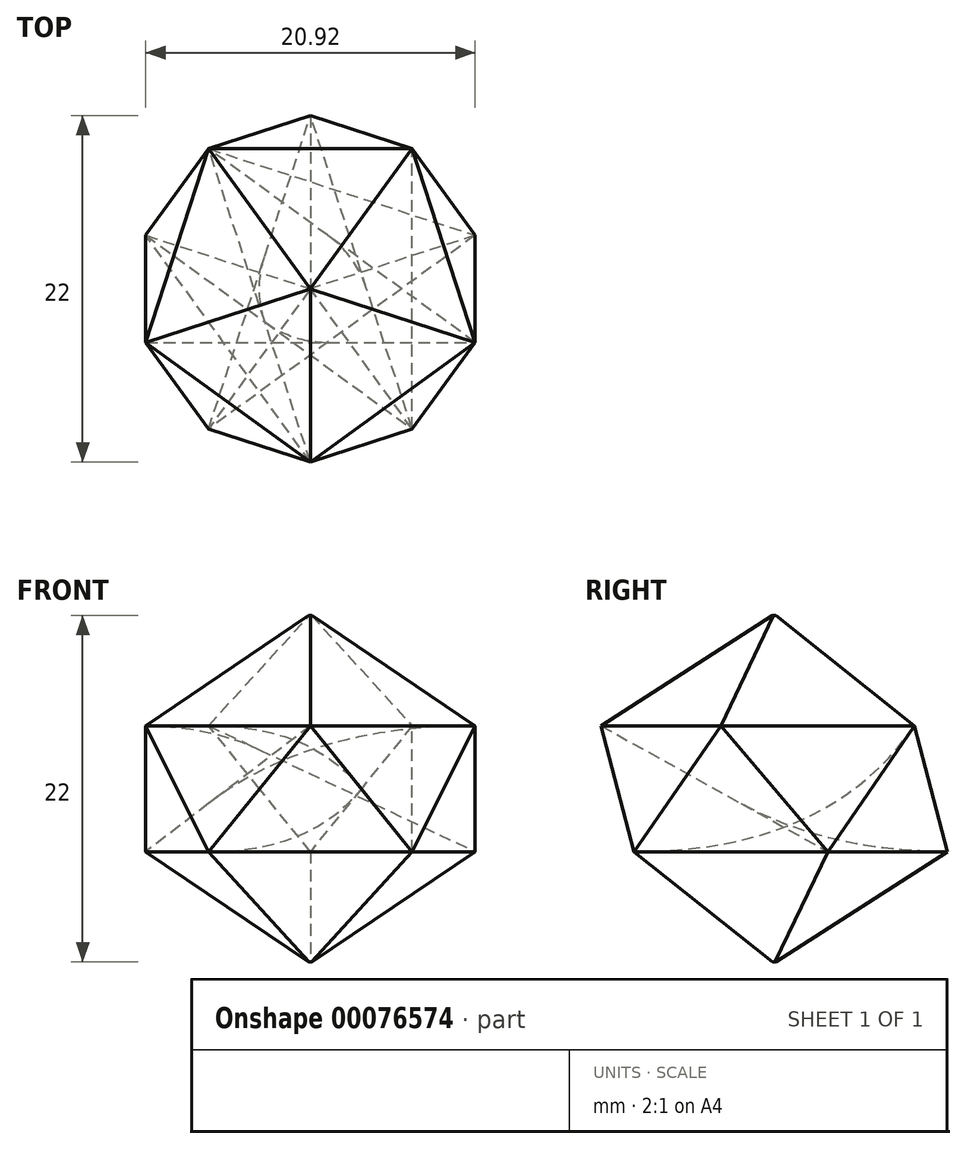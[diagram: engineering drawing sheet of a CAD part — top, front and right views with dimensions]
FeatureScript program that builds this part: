
annotation { "Feature Type Name" : "Feature", "Feature Type Description" : "" }
export const myFeature = defineFeature(function(context is Context, id is Id, definition is map)
    precondition{}
    {
        {
            var Q0;
            Q0=qCreatedBy(makeId("Top.planeOp"),FACE);
            var sketch = newSketch(context, id + "F0", { "sketchPlane" : qUnion([Q0])});
            skCircle(sketch, "E0.cCircle", {"center": v(0, 0) * mm, "radius": 11 * mm, "construction": true});
            skLineSegment(sketch, "E0.0", {"start": v(-6.47, 8.9) * mm, "end": v(6.47, 8.9) * mm});
            skLineSegment(sketch, "E0.1", {"start": v(6.47, 8.9) * mm, "end": v(10.46, -3.4) * mm});
            skLineSegment(sketch, "E0.2", {"start": v(10.46, -3.4) * mm, "end": v(0, -11) * mm});
            skLineSegment(sketch, "E0.3", {"start": v(0, -11) * mm, "end": v(-10.46, -3.4) * mm});
            skLineSegment(sketch, "E0.4", {"start": v(-10.46, -3.4) * mm, "end": v(-6.47, 8.9) * mm});
            skSolve(sketch);
        }
        {
            var Q0;
            Q0=makeQuery(id+"F0.imprint","IMPRINT",FACE,{"disambiguationData":[TD([[makeQuery(id+"F0.imprint","IMPRINT",EDGE,{"derivedFrom":sQuery(id+"F0.wireOp",EDGE,"E0.0")}),-1.0]])]});
            extrude(context, id + "F1", {"entities" : qUnion([Q0]), "depth" : 7 * mm});
        }
        {
            var Q0;
            Q0=makeQuery(id+"F1.opExtrude","CAP_FACE",FACE,{"disambiguationData":[OSD([sQuery(id+"F0.wireOp",EDGE,"E0.0"),sQuery(id+"F0.wireOp",EDGE,"E0.1"),sQuery(id+"F0.wireOp",EDGE,"E0.2"),sQuery(id+"F0.wireOp",EDGE,"E0.3"),sQuery(id+"F0.wireOp",EDGE,"E0.4")])],"isStart":false});
            chamfer(context, id + "F2", {"entities" : qUnion([Q0]), "chamferType" : ChamferType.TWO_OFFSETS, "width1" : 7 * mm, "oppositeDirection" : false, "width2" : 8.8 * mm, "tangentPropagation" : true});
        }
        {
            var Q0;
            Q0=qCreatedBy(makeId("Top.planeOp"),FACE);
            cPlane(context, id + "F3", {"entities" : qUnion([Q0]), "cplaneType" : CPlaneType.OFFSET, "offset" : 8 * mm, "oppositeDirection" : true, "width" : 150 * mm, "height" : 150 * mm});
        }
        {
            var Q0;
            Q0=qCreatedBy(id+"F3.planeOp",FACE);
            var sketch = newSketch(context, id + "F4", { "sketchPlane" : qUnion([Q0])});
            skCircle(sketch, "E1.cCircle", {"center": v(0, 0) * mm, "radius": 11 * mm, "construction": true});
            skLineSegment(sketch, "E1.0", {"start": v(-6.47, -8.9) * mm, "end": v(-10.46, 3.4) * mm});
            skLineSegment(sketch, "E1.1", {"start": v(-10.46, 3.4) * mm, "end": v(0, 11) * mm});
            skLineSegment(sketch, "E1.2", {"start": v(0, 11) * mm, "end": v(10.46, 3.4) * mm});
            skLineSegment(sketch, "E1.3", {"start": v(10.46, 3.4) * mm, "end": v(6.47, -8.9) * mm});
            skLineSegment(sketch, "E1.4", {"start": v(6.47, -8.9) * mm, "end": v(-6.47, -8.9) * mm});
            skSolve(sketch);
        }
        {
            var Q0;
            Q0=makeQuery(id+"F4.imprint","IMPRINT",FACE,{"disambiguationData":[TD([[makeQuery(id+"F4.imprint","IMPRINT",EDGE,{"derivedFrom":sQuery(id+"F4.wireOp",EDGE,"E1.0")}),-1.0]])]});
            extrude(context, id + "F5", {"entities" : qUnion([Q0]), "oppositeDirection" : true, "depth" : 7 * mm});
        }
        {
            var Q0;
            Q0=makeQuery(id+"F5.opExtrude","CAP_FACE",FACE,{"disambiguationData":[OSD([sQuery(id+"F4.wireOp",EDGE,"E1.0"),sQuery(id+"F4.wireOp",EDGE,"E1.1"),sQuery(id+"F4.wireOp",EDGE,"E1.2"),sQuery(id+"F4.wireOp",EDGE,"E1.3"),sQuery(id+"F4.wireOp",EDGE,"E1.4")])],"isStart":false});
            chamfer(context, id + "F6", {"entities" : qUnion([Q0]), "chamferType" : ChamferType.TWO_OFFSETS, "width1" : 8.8 * mm, "oppositeDirection" : false, "width2" : 7 * mm, "tangentPropagation" : true});
        }
        {
            var Q0;
            {var subQ0=sQuery(id+"F4.wireOp",EDGE,"E1.3");var subQ1=sQuery(id+"F4.wireOp",EDGE,"E1.2");Q0=makeQuery(id+"F6.opChamfer","BLEND_VERTEX",VERTEX,{"blendedFrom":[makeQuery(id+"F5.opExtrude","CAP_EDGE",EDGE,{"disambiguationData":[OSD([subQ1])],"isStart":false}),makeQuery(id+"F5.opExtrude","CAP_EDGE",EDGE,{"disambiguationData":[OSD([subQ0])],"isStart":false}),makeQuery(id+"F5.opExtrude","CAP_FACE",FACE,{"disambiguationData":[OSD([sQuery(id+"F4.wireOp",EDGE,"E1.0"),sQuery(id+"F4.wireOp",EDGE,"E1.1"),subQ1,subQ0,sQuery(id+"F4.wireOp",EDGE,"E1.4")])],"isStart":true})],"blendedInto":[makeQuery(id+"F5.opExtrude","CAP_FACE",FACE,{"disambiguationData":[OSD([sQuery(id+"F4.wireOp",EDGE,"E1.0"),sQuery(id+"F4.wireOp",EDGE,"E1.1"),subQ1,subQ0,sQuery(id+"F4.wireOp",EDGE,"E1.4")])],"isStart":true})]});}
            var Q1;
            {var subQ0=sQuery(id+"F0.wireOp",EDGE,"E0.2");var subQ1=sQuery(id+"F0.wireOp",EDGE,"E0.1");Q1=makeQuery(id+"F2.opChamfer","BLEND_VERTEX",VERTEX,{"blendedFrom":[makeQuery(id+"F1.opExtrude","CAP_EDGE",EDGE,{"disambiguationData":[OSD([subQ1])],"isStart":false}),makeQuery(id+"F1.opExtrude","CAP_EDGE",EDGE,{"disambiguationData":[OSD([subQ0])],"isStart":false}),makeQuery(id+"F1.opExtrude","CAP_FACE",FACE,{"disambiguationData":[OSD([sQuery(id+"F0.wireOp",EDGE,"E0.0"),subQ1,subQ0,sQuery(id+"F0.wireOp",EDGE,"E0.3"),sQuery(id+"F0.wireOp",EDGE,"E0.4")])],"isStart":true})],"blendedInto":[makeQuery(id+"F1.opExtrude","CAP_FACE",FACE,{"disambiguationData":[OSD([sQuery(id+"F0.wireOp",EDGE,"E0.0"),subQ1,subQ0,sQuery(id+"F0.wireOp",EDGE,"E0.3"),sQuery(id+"F0.wireOp",EDGE,"E0.4")])],"isStart":true})]});}
            var Q2;
            {var subQ0=sQuery(id+"F0.wireOp",EDGE,"E0.1");var subQ1=sQuery(id+"F0.wireOp",EDGE,"E0.0");Q2=makeQuery(id+"F2.opChamfer","BLEND_VERTEX",VERTEX,{"blendedFrom":[makeQuery(id+"F1.opExtrude","CAP_EDGE",EDGE,{"disambiguationData":[OSD([subQ1])],"isStart":false}),makeQuery(id+"F1.opExtrude","CAP_EDGE",EDGE,{"disambiguationData":[OSD([subQ0])],"isStart":false}),makeQuery(id+"F1.opExtrude","CAP_FACE",FACE,{"disambiguationData":[OSD([subQ1,subQ0,sQuery(id+"F0.wireOp",EDGE,"E0.2"),sQuery(id+"F0.wireOp",EDGE,"E0.3"),sQuery(id+"F0.wireOp",EDGE,"E0.4")])],"isStart":true})],"blendedInto":[makeQuery(id+"F1.opExtrude","CAP_FACE",FACE,{"disambiguationData":[OSD([subQ1,subQ0,sQuery(id+"F0.wireOp",EDGE,"E0.2"),sQuery(id+"F0.wireOp",EDGE,"E0.3"),sQuery(id+"F0.wireOp",EDGE,"E0.4")])],"isStart":true})]});}
            cPlane(context, id + "F7", {"entities" : qUnion([Q0, Q1, Q2]), "cplaneType" : CPlaneType.THREE_POINT, "offset" : 150 * mm, "width" : 150 * mm, "height" : 150 * mm});
        }
        {
            var Q0;
            Q0=qCreatedBy(id+"F7.planeOp",FACE);
            var sketch = newSketch(context, id + "F8", { "sketchPlane" : qUnion([Q0])});
            skLineSegment(sketch, "E2", {"start": v(6.63, -1.72) * mm, "end": v(0.87, -10.5) * mm});
            skLineSegment(sketch, "E3", {"start": v(0.87, -10.5) * mm, "end": v(-6.26, -2.78) * mm});
            skLineSegment(sketch, "E4", {"start": v(-6.26, -2.78) * mm, "end": v(6.63, -1.72) * mm});
            skSolve(sketch);
        }
        {
            var Q0;
            {var subQ0=sQuery(id+"F4.wireOp",EDGE,"E1.4");var subQ1=sQuery(id+"F4.wireOp",EDGE,"E1.0");Q0=makeQuery(id+"F6.opChamfer","BLEND_VERTEX",VERTEX,{"blendedFrom":[makeQuery(id+"F5.opExtrude","CAP_EDGE",EDGE,{"disambiguationData":[OSD([subQ1])],"isStart":false}),makeQuery(id+"F5.opExtrude","CAP_EDGE",EDGE,{"disambiguationData":[OSD([subQ0])],"isStart":false}),makeQuery(id+"F5.opExtrude","CAP_FACE",FACE,{"disambiguationData":[OSD([subQ1,sQuery(id+"F4.wireOp",EDGE,"E1.1"),sQuery(id+"F4.wireOp",EDGE,"E1.2"),sQuery(id+"F4.wireOp",EDGE,"E1.3"),subQ0])],"isStart":true})],"blendedInto":[makeQuery(id+"F5.opExtrude","CAP_FACE",FACE,{"disambiguationData":[OSD([subQ1,sQuery(id+"F4.wireOp",EDGE,"E1.1"),sQuery(id+"F4.wireOp",EDGE,"E1.2"),sQuery(id+"F4.wireOp",EDGE,"E1.3"),subQ0])],"isStart":true})]});}
            var Q1;
            {var subQ0=sQuery(id+"F0.wireOp",EDGE,"E0.3");var subQ1=sQuery(id+"F0.wireOp",EDGE,"E0.2");Q1=makeQuery(id+"F2.opChamfer","BLEND_VERTEX",VERTEX,{"blendedFrom":[makeQuery(id+"F1.opExtrude","CAP_EDGE",EDGE,{"disambiguationData":[OSD([subQ1])],"isStart":false}),makeQuery(id+"F1.opExtrude","CAP_EDGE",EDGE,{"disambiguationData":[OSD([subQ0])],"isStart":false}),makeQuery(id+"F1.opExtrude","CAP_FACE",FACE,{"disambiguationData":[OSD([sQuery(id+"F0.wireOp",EDGE,"E0.0"),sQuery(id+"F0.wireOp",EDGE,"E0.1"),subQ1,subQ0,sQuery(id+"F0.wireOp",EDGE,"E0.4")])],"isStart":true})],"blendedInto":[makeQuery(id+"F1.opExtrude","CAP_FACE",FACE,{"disambiguationData":[OSD([sQuery(id+"F0.wireOp",EDGE,"E0.0"),sQuery(id+"F0.wireOp",EDGE,"E0.1"),subQ1,subQ0,sQuery(id+"F0.wireOp",EDGE,"E0.4")])],"isStart":true})]});}
            var Q2;
            {var subQ0=sQuery(id+"F0.wireOp",EDGE,"E0.4");var subQ1=sQuery(id+"F0.wireOp",EDGE,"E0.3");Q2=makeQuery(id+"F2.opChamfer","BLEND_VERTEX",VERTEX,{"blendedFrom":[makeQuery(id+"F1.opExtrude","CAP_EDGE",EDGE,{"disambiguationData":[OSD([subQ1])],"isStart":false}),makeQuery(id+"F1.opExtrude","CAP_EDGE",EDGE,{"disambiguationData":[OSD([subQ0])],"isStart":false}),makeQuery(id+"F1.opExtrude","CAP_FACE",FACE,{"disambiguationData":[OSD([sQuery(id+"F0.wireOp",EDGE,"E0.0"),sQuery(id+"F0.wireOp",EDGE,"E0.1"),sQuery(id+"F0.wireOp",EDGE,"E0.2"),subQ1,subQ0])],"isStart":true})],"blendedInto":[makeQuery(id+"F1.opExtrude","CAP_FACE",FACE,{"disambiguationData":[OSD([sQuery(id+"F0.wireOp",EDGE,"E0.0"),sQuery(id+"F0.wireOp",EDGE,"E0.1"),sQuery(id+"F0.wireOp",EDGE,"E0.2"),subQ1,subQ0])],"isStart":true})]});}
            cPlane(context, id + "F9", {"entities" : qUnion([Q0, Q1, Q2]), "cplaneType" : CPlaneType.THREE_POINT, "offset" : 150 * mm, "width" : 150 * mm, "height" : 150 * mm});
        }
        {
            var Q0;
            Q0=qCreatedBy(id+"F9.planeOp",FACE);
            var sketch = newSketch(context, id + "F10", { "sketchPlane" : qUnion([Q0])});
            skLineSegment(sketch, "E5", {"start": v(6.77, -1.05) * mm, "end": v(1.91, -10.36) * mm});
            skLineSegment(sketch, "E6", {"start": v(1.91, -10.36) * mm, "end": v(-5.95, -3.4) * mm});
            skLineSegment(sketch, "E7", {"start": v(-5.95, -3.4) * mm, "end": v(6.77, -1.05) * mm});
            skSolve(sketch);
        }
        {
            var Q1;
            Q1=makeQuery(id+"F8.imprint","IMPRINT",FACE,{"disambiguationData":[TD([[makeQuery(id+"F8.imprint","IMPRINT",EDGE,{"derivedFrom":sQuery(id+"F8.wireOp",EDGE,"E2")}),-1.0]])]});
            var Q2;
            Q2=makeQuery(id+"F10.imprint","IMPRINT",FACE,{"disambiguationData":[TD([[makeQuery(id+"F10.imprint","IMPRINT",EDGE,{"derivedFrom":sQuery(id+"F10.wireOp",EDGE,"E5")}),-1.0]])]});
            loft(context, id + "F11", {"operationType" : NewBodyOperationType.ADD, "sheetProfilesArray" : [{ "sheetProfileEntities" : qUnion([Q1]) }, { "sheetProfileEntities" : qUnion([Q2]) }]});
        }
        {
            var Q0;
            {var subQ0=sQuery(id+"F0.wireOp",EDGE,"E0.3");var subQ1=sQuery(id+"F0.wireOp",EDGE,"E0.2");Q0=makeQuery(id+"F11.boolean.opBoolean","MERGE",VERTEX,{"derivedFrom":[makeQuery(id+"F2.opChamfer","BLEND_VERTEX",VERTEX,{"blendedFrom":[makeQuery(id+"F1.opExtrude","CAP_EDGE",EDGE,{"disambiguationData":[OSD([subQ1])],"isStart":false}),makeQuery(id+"F1.opExtrude","CAP_EDGE",EDGE,{"disambiguationData":[OSD([subQ0])],"isStart":false}),makeQuery(id+"F1.opExtrude","CAP_FACE",FACE,{"disambiguationData":[OSD([sQuery(id+"F0.wireOp",EDGE,"E0.0"),sQuery(id+"F0.wireOp",EDGE,"E0.1"),subQ1,subQ0,sQuery(id+"F0.wireOp",EDGE,"E0.4")])],"isStart":true})],"blendedInto":[makeQuery(id+"F1.opExtrude","CAP_FACE",FACE,{"disambiguationData":[OSD([sQuery(id+"F0.wireOp",EDGE,"E0.0"),sQuery(id+"F0.wireOp",EDGE,"E0.1"),subQ1,subQ0,sQuery(id+"F0.wireOp",EDGE,"E0.4")])],"isStart":true})]}),makeQuery(id+"F11.opLoft","MID_CAP_VERTEX",VERTEX,{"disambiguationData":[OSD([sQuery(id+"F10.wireOp",EDGE,"E6"),sQuery(id+"F10.wireOp",EDGE,"E7")])],"capPos":1.0})]});}
            var Q1;
            {var subQ0=sQuery(id+"F4.wireOp",EDGE,"E1.4");var subQ1=sQuery(id+"F4.wireOp",EDGE,"E1.3");Q1=makeQuery(id+"F6.opChamfer","BLEND_VERTEX",VERTEX,{"blendedFrom":[makeQuery(id+"F5.opExtrude","CAP_EDGE",EDGE,{"disambiguationData":[OSD([subQ1])],"isStart":false}),makeQuery(id+"F5.opExtrude","CAP_EDGE",EDGE,{"disambiguationData":[OSD([subQ0])],"isStart":false}),makeQuery(id+"F5.opExtrude","CAP_FACE",FACE,{"disambiguationData":[OSD([sQuery(id+"F4.wireOp",EDGE,"E1.0"),sQuery(id+"F4.wireOp",EDGE,"E1.1"),sQuery(id+"F4.wireOp",EDGE,"E1.2"),subQ1,subQ0])],"isStart":true})],"blendedInto":[makeQuery(id+"F5.opExtrude","CAP_FACE",FACE,{"disambiguationData":[OSD([sQuery(id+"F4.wireOp",EDGE,"E1.0"),sQuery(id+"F4.wireOp",EDGE,"E1.1"),sQuery(id+"F4.wireOp",EDGE,"E1.2"),subQ1,subQ0])],"isStart":true})]});}
            var Q2;
            Q2=makeQuery(id+"F11.opLoft","MID_CAP_VERTEX",VERTEX,{"disambiguationData":[OSD([sQuery(id+"F10.wireOp",EDGE,"E5"),sQuery(id+"F10.wireOp",EDGE,"E6")])],"capPos":1.0});
            cPlane(context, id + "F12", {"entities" : qUnion([Q0, Q1, Q2]), "cplaneType" : CPlaneType.THREE_POINT, "offset" : 150 * mm, "width" : 150 * mm, "height" : 150 * mm});
        }
        {
            var Q0;
            Q0=qCreatedBy(id+"F12.planeOp",FACE);
            var sketch = newSketch(context, id + "F13", { "sketchPlane" : qUnion([Q0])});
            skLineSegment(sketch, "E8", {"start": v(6.47, -5.48) * mm, "end": v(0, 2.8) * mm});
            skLineSegment(sketch, "E9", {"start": v(0, 2.8) * mm, "end": v(-6.47, -5.48) * mm});
            skLineSegment(sketch, "E10", {"start": v(-6.47, -5.48) * mm, "end": v(6.47, -5.48) * mm});
            skSolve(sketch);
        }
        {
            var Q0;
            {var subQ0=sQuery(id+"F0.wireOp",EDGE,"E0.1");var subQ1=sQuery(id+"F0.wireOp",EDGE,"E0.0");Q0=makeQuery(id+"F11.boolean.opBoolean","MERGE",VERTEX,{"derivedFrom":[makeQuery(id+"F2.opChamfer","BLEND_VERTEX",VERTEX,{"blendedFrom":[makeQuery(id+"F1.opExtrude","CAP_EDGE",EDGE,{"disambiguationData":[OSD([subQ1])],"isStart":false}),makeQuery(id+"F1.opExtrude","CAP_EDGE",EDGE,{"disambiguationData":[OSD([subQ0])],"isStart":false}),makeQuery(id+"F1.opExtrude","CAP_FACE",FACE,{"disambiguationData":[OSD([subQ1,subQ0,sQuery(id+"F0.wireOp",EDGE,"E0.2"),sQuery(id+"F0.wireOp",EDGE,"E0.3"),sQuery(id+"F0.wireOp",EDGE,"E0.4")])],"isStart":true})],"blendedInto":[makeQuery(id+"F1.opExtrude","CAP_FACE",FACE,{"disambiguationData":[OSD([subQ1,subQ0,sQuery(id+"F0.wireOp",EDGE,"E0.2"),sQuery(id+"F0.wireOp",EDGE,"E0.3"),sQuery(id+"F0.wireOp",EDGE,"E0.4")])],"isStart":true})]}),makeQuery(id+"F11.opLoft","MID_CAP_VERTEX",VERTEX,{"disambiguationData":[OSD([sQuery(id+"F8.wireOp",EDGE,"E2"),sQuery(id+"F8.wireOp",EDGE,"E4")])],"capPos":0.0})]});}
            var Q1;
            {var subQ0=sQuery(id+"F0.wireOp",EDGE,"E0.4");var subQ1=sQuery(id+"F0.wireOp",EDGE,"E0.0");Q1=makeQuery(id+"F2.opChamfer","BLEND_VERTEX",VERTEX,{"blendedFrom":[makeQuery(id+"F1.opExtrude","CAP_EDGE",EDGE,{"disambiguationData":[OSD([subQ1])],"isStart":false}),makeQuery(id+"F1.opExtrude","CAP_EDGE",EDGE,{"disambiguationData":[OSD([subQ0])],"isStart":false}),makeQuery(id+"F1.opExtrude","CAP_FACE",FACE,{"disambiguationData":[OSD([subQ1,sQuery(id+"F0.wireOp",EDGE,"E0.1"),sQuery(id+"F0.wireOp",EDGE,"E0.2"),sQuery(id+"F0.wireOp",EDGE,"E0.3"),subQ0])],"isStart":true})],"blendedInto":[makeQuery(id+"F1.opExtrude","CAP_FACE",FACE,{"disambiguationData":[OSD([subQ1,sQuery(id+"F0.wireOp",EDGE,"E0.1"),sQuery(id+"F0.wireOp",EDGE,"E0.2"),sQuery(id+"F0.wireOp",EDGE,"E0.3"),subQ0])],"isStart":true})]});}
            var Q2;
            {var subQ0=sQuery(id+"F4.wireOp",EDGE,"E1.2");var subQ1=sQuery(id+"F4.wireOp",EDGE,"E1.1");Q2=makeQuery(id+"F6.opChamfer","BLEND_VERTEX",VERTEX,{"blendedFrom":[makeQuery(id+"F5.opExtrude","CAP_EDGE",EDGE,{"disambiguationData":[OSD([subQ1])],"isStart":false}),makeQuery(id+"F5.opExtrude","CAP_EDGE",EDGE,{"disambiguationData":[OSD([subQ0])],"isStart":false}),makeQuery(id+"F5.opExtrude","CAP_FACE",FACE,{"disambiguationData":[OSD([sQuery(id+"F4.wireOp",EDGE,"E1.0"),subQ1,subQ0,sQuery(id+"F4.wireOp",EDGE,"E1.3"),sQuery(id+"F4.wireOp",EDGE,"E1.4")])],"isStart":true})],"blendedInto":[makeQuery(id+"F5.opExtrude","CAP_FACE",FACE,{"disambiguationData":[OSD([sQuery(id+"F4.wireOp",EDGE,"E1.0"),subQ1,subQ0,sQuery(id+"F4.wireOp",EDGE,"E1.3"),sQuery(id+"F4.wireOp",EDGE,"E1.4")])],"isStart":true})]});}
            cPlane(context, id + "F14", {"entities" : qUnion([Q0, Q1, Q2]), "cplaneType" : CPlaneType.THREE_POINT, "offset" : 150 * mm, "width" : 150 * mm, "height" : 150 * mm});
        }
        {
            var Q0;
            Q0=qCreatedBy(id+"F14.planeOp",FACE);
            var sketch = newSketch(context, id + "F15", { "sketchPlane" : qUnion([Q0])});
            skLineSegment(sketch, "E11", {"start": v(-6.47, -2.26) * mm, "end": v(0, -10.53) * mm});
            skLineSegment(sketch, "E12", {"start": v(0, -10.53) * mm, "end": v(6.47, -2.26) * mm});
            skLineSegment(sketch, "E13", {"start": v(6.47, -2.26) * mm, "end": v(-6.47, -2.26) * mm});
            skSolve(sketch);
        }
        {
            var Q1;
            Q1=makeQuery(id+"F13.imprint","IMPRINT",FACE,{"disambiguationData":[TD([[makeQuery(id+"F13.imprint","IMPRINT",EDGE,{"derivedFrom":sQuery(id+"F13.wireOp",EDGE,"E8")}),1.0]])]});
            var Q2;
            Q2=makeQuery(id+"F15.imprint","IMPRINT",FACE,{"disambiguationData":[TD([[makeQuery(id+"F15.imprint","IMPRINT",EDGE,{"derivedFrom":sQuery(id+"F15.wireOp",EDGE,"E11")}),1.0]])]});
            loft(context, id + "F16", {"sheetProfilesArray" : [{ "sheetProfileEntities" : qUnion([Q1]) }, { "sheetProfileEntities" : qUnion([Q2]) }]});
        }
        {
            var Q0;
            {var subQ0=sQuery(id+"F0.wireOp",EDGE,"E0.1");var subQ1=sQuery(id+"F0.wireOp",EDGE,"E0.0");Q0=makeQuery(id+"F11.boolean.opBoolean","MERGE",VERTEX,{"derivedFrom":[makeQuery(id+"F2.opChamfer","BLEND_VERTEX",VERTEX,{"blendedFrom":[makeQuery(id+"F1.opExtrude","CAP_EDGE",EDGE,{"disambiguationData":[OSD([subQ1])],"isStart":false}),makeQuery(id+"F1.opExtrude","CAP_EDGE",EDGE,{"disambiguationData":[OSD([subQ0])],"isStart":false}),makeQuery(id+"F1.opExtrude","CAP_FACE",FACE,{"disambiguationData":[OSD([subQ1,subQ0,sQuery(id+"F0.wireOp",EDGE,"E0.2"),sQuery(id+"F0.wireOp",EDGE,"E0.3"),sQuery(id+"F0.wireOp",EDGE,"E0.4")])],"isStart":true})],"blendedInto":[makeQuery(id+"F1.opExtrude","CAP_FACE",FACE,{"disambiguationData":[OSD([subQ1,subQ0,sQuery(id+"F0.wireOp",EDGE,"E0.2"),sQuery(id+"F0.wireOp",EDGE,"E0.3"),sQuery(id+"F0.wireOp",EDGE,"E0.4")])],"isStart":true})]}),makeQuery(id+"F11.opLoft","MID_CAP_VERTEX",VERTEX,{"disambiguationData":[OSD([sQuery(id+"F8.wireOp",EDGE,"E2"),sQuery(id+"F8.wireOp",EDGE,"E4")])],"capPos":0.0})]});}
            var Q1;
            Q1=makeQuery(id+"F11.opLoft","MID_CAP_VERTEX",VERTEX,{"disambiguationData":[OSD([sQuery(id+"F8.wireOp",EDGE,"E2"),sQuery(id+"F8.wireOp",EDGE,"E3")])],"capPos":0.0});
            var Q2;
            {var subQ0=sQuery(id+"F4.wireOp",EDGE,"E1.2");var subQ1=sQuery(id+"F4.wireOp",EDGE,"E1.1");Q2=makeQuery(id+"F6.opChamfer","BLEND_VERTEX",VERTEX,{"blendedFrom":[makeQuery(id+"F5.opExtrude","CAP_EDGE",EDGE,{"disambiguationData":[OSD([subQ1])],"isStart":false}),makeQuery(id+"F5.opExtrude","CAP_EDGE",EDGE,{"disambiguationData":[OSD([subQ0])],"isStart":false}),makeQuery(id+"F5.opExtrude","CAP_FACE",FACE,{"disambiguationData":[OSD([sQuery(id+"F4.wireOp",EDGE,"E1.0"),subQ1,subQ0,sQuery(id+"F4.wireOp",EDGE,"E1.3"),sQuery(id+"F4.wireOp",EDGE,"E1.4")])],"isStart":true})],"blendedInto":[makeQuery(id+"F5.opExtrude","CAP_FACE",FACE,{"disambiguationData":[OSD([sQuery(id+"F4.wireOp",EDGE,"E1.0"),subQ1,subQ0,sQuery(id+"F4.wireOp",EDGE,"E1.3"),sQuery(id+"F4.wireOp",EDGE,"E1.4")])],"isStart":true})]});}
            cPlane(context, id + "F17", {"entities" : qUnion([Q0, Q1, Q2]), "cplaneType" : CPlaneType.THREE_POINT, "offset" : 150 * mm, "width" : 150 * mm, "height" : 150 * mm});
        }
        {
            var Q0;
            Q0=qCreatedBy(id+"F17.planeOp",FACE);
            var sketch = newSketch(context, id + "F18", { "sketchPlane" : qUnion([Q0])});
            skLineSegment(sketch, "E14", {"start": v(5.36, -6.56) * mm, "end": v(-7.35, -4.21) * mm});
            skLineSegment(sketch, "E15", {"start": v(-7.35, -4.21) * mm, "end": v(0.5, 2.75) * mm});
            skLineSegment(sketch, "E16", {"start": v(0.5, 2.75) * mm, "end": v(5.36, -6.56) * mm});
            skSolve(sketch);
        }
        {
            var Q0;
            {var subQ0=sQuery(id+"F0.wireOp",EDGE,"E0.4");var subQ1=sQuery(id+"F0.wireOp",EDGE,"E0.3");Q0=makeQuery(id+"F11.boolean.opBoolean","MERGE",VERTEX,{"derivedFrom":[makeQuery(id+"F2.opChamfer","BLEND_VERTEX",VERTEX,{"blendedFrom":[makeQuery(id+"F1.opExtrude","CAP_EDGE",EDGE,{"disambiguationData":[OSD([subQ1])],"isStart":false}),makeQuery(id+"F1.opExtrude","CAP_EDGE",EDGE,{"disambiguationData":[OSD([subQ0])],"isStart":false}),makeQuery(id+"F1.opExtrude","CAP_FACE",FACE,{"disambiguationData":[OSD([sQuery(id+"F0.wireOp",EDGE,"E0.0"),sQuery(id+"F0.wireOp",EDGE,"E0.1"),sQuery(id+"F0.wireOp",EDGE,"E0.2"),subQ1,subQ0])],"isStart":true})],"blendedInto":[makeQuery(id+"F1.opExtrude","CAP_FACE",FACE,{"disambiguationData":[OSD([sQuery(id+"F0.wireOp",EDGE,"E0.0"),sQuery(id+"F0.wireOp",EDGE,"E0.1"),sQuery(id+"F0.wireOp",EDGE,"E0.2"),subQ1,subQ0])],"isStart":true})]}),makeQuery(id+"F11.opLoft","MID_CAP_VERTEX",VERTEX,{"disambiguationData":[OSD([sQuery(id+"F10.wireOp",EDGE,"E5"),sQuery(id+"F10.wireOp",EDGE,"E7")])],"capPos":1.0})]});}
            var Q1;
            Q1=makeQuery(id+"F11.opLoft","MID_CAP_VERTEX",VERTEX,{"disambiguationData":[OSD([sQuery(id+"F10.wireOp",EDGE,"E5"),sQuery(id+"F10.wireOp",EDGE,"E6")])],"capPos":1.0});
            var Q2;
            {var subQ0=sQuery(id+"F4.wireOp",EDGE,"E1.1");var subQ1=sQuery(id+"F4.wireOp",EDGE,"E1.0");Q2=makeQuery(id+"F6.opChamfer","BLEND_VERTEX",VERTEX,{"blendedFrom":[makeQuery(id+"F5.opExtrude","CAP_EDGE",EDGE,{"disambiguationData":[OSD([subQ1])],"isStart":false}),makeQuery(id+"F5.opExtrude","CAP_EDGE",EDGE,{"disambiguationData":[OSD([subQ0])],"isStart":false}),makeQuery(id+"F5.opExtrude","CAP_FACE",FACE,{"disambiguationData":[OSD([subQ1,subQ0,sQuery(id+"F4.wireOp",EDGE,"E1.2"),sQuery(id+"F4.wireOp",EDGE,"E1.3"),sQuery(id+"F4.wireOp",EDGE,"E1.4")])],"isStart":true})],"blendedInto":[makeQuery(id+"F5.opExtrude","CAP_FACE",FACE,{"disambiguationData":[OSD([subQ1,subQ0,sQuery(id+"F4.wireOp",EDGE,"E1.2"),sQuery(id+"F4.wireOp",EDGE,"E1.3"),sQuery(id+"F4.wireOp",EDGE,"E1.4")])],"isStart":true})]});}
            cPlane(context, id + "F19", {"entities" : qUnion([Q0, Q1, Q2]), "cplaneType" : CPlaneType.THREE_POINT, "offset" : 150 * mm, "width" : 150 * mm, "height" : 150 * mm});
        }
        {
            var Q0;
            Q0=qCreatedBy(id+"F19.planeOp",FACE);
            var sketch = newSketch(context, id + "F20", { "sketchPlane" : qUnion([Q0])});
            skLineSegment(sketch, "E17", {"start": v(0.23, 2.78) * mm, "end": v(-6.9, -4.93) * mm});
            skLineSegment(sketch, "E18", {"start": v(-6.9, -4.93) * mm, "end": v(6, -6) * mm});
            skLineSegment(sketch, "E19", {"start": v(6, -6) * mm, "end": v(0.23, 2.78) * mm});
            skSolve(sketch);
        }
        {
            var Q0;
            Q0 = qSketchRegion(id + "F18", true);
            var Q1;
            Q1 = qSketchRegion(id + "F20", true);
            loft(context, id + "F21", {"sheetProfilesArray" : [{ "sheetProfileEntities" : qUnion([Q0]) }, { "sheetProfileEntities" : qUnion([Q1]) }]});
        }
        {
            var Q0;
            {var subQ0=sQuery(id+"F0.wireOp",EDGE,"E0.4");var subQ1=sQuery(id+"F0.wireOp",EDGE,"E0.0");Q0=makeQuery(id+"F2.opChamfer","BLEND_VERTEX",VERTEX,{"blendedFrom":[makeQuery(id+"F1.opExtrude","CAP_EDGE",EDGE,{"disambiguationData":[OSD([subQ1])],"isStart":false}),makeQuery(id+"F1.opExtrude","CAP_EDGE",EDGE,{"disambiguationData":[OSD([subQ0])],"isStart":false}),makeQuery(id+"F1.opExtrude","CAP_FACE",FACE,{"disambiguationData":[OSD([subQ1,sQuery(id+"F0.wireOp",EDGE,"E0.1"),sQuery(id+"F0.wireOp",EDGE,"E0.2"),sQuery(id+"F0.wireOp",EDGE,"E0.3"),subQ0])],"isStart":true})],"blendedInto":[makeQuery(id+"F1.opExtrude","CAP_FACE",FACE,{"disambiguationData":[OSD([subQ1,sQuery(id+"F0.wireOp",EDGE,"E0.1"),sQuery(id+"F0.wireOp",EDGE,"E0.2"),sQuery(id+"F0.wireOp",EDGE,"E0.3"),subQ0])],"isStart":true})]});}
            var Q1;
            {var subQ0=sQuery(id+"F0.wireOp",EDGE,"E0.4");var subQ1=sQuery(id+"F0.wireOp",EDGE,"E0.3");Q1=makeQuery(id+"F11.boolean.opBoolean","MERGE",VERTEX,{"derivedFrom":[makeQuery(id+"F2.opChamfer","BLEND_VERTEX",VERTEX,{"blendedFrom":[makeQuery(id+"F1.opExtrude","CAP_EDGE",EDGE,{"disambiguationData":[OSD([subQ1])],"isStart":false}),makeQuery(id+"F1.opExtrude","CAP_EDGE",EDGE,{"disambiguationData":[OSD([subQ0])],"isStart":false}),makeQuery(id+"F1.opExtrude","CAP_FACE",FACE,{"disambiguationData":[OSD([sQuery(id+"F0.wireOp",EDGE,"E0.0"),sQuery(id+"F0.wireOp",EDGE,"E0.1"),sQuery(id+"F0.wireOp",EDGE,"E0.2"),subQ1,subQ0])],"isStart":true})],"blendedInto":[makeQuery(id+"F1.opExtrude","CAP_FACE",FACE,{"disambiguationData":[OSD([sQuery(id+"F0.wireOp",EDGE,"E0.0"),sQuery(id+"F0.wireOp",EDGE,"E0.1"),sQuery(id+"F0.wireOp",EDGE,"E0.2"),subQ1,subQ0])],"isStart":true})]}),makeQuery(id+"F11.opLoft","MID_CAP_VERTEX",VERTEX,{"disambiguationData":[OSD([sQuery(id+"F10.wireOp",EDGE,"E5"),sQuery(id+"F10.wireOp",EDGE,"E7")])],"capPos":1.0})]});}
            var Q2;
            {var subQ0=sQuery(id+"F4.wireOp",EDGE,"E1.1");var subQ1=sQuery(id+"F4.wireOp",EDGE,"E1.0");Q2=makeQuery(id+"F6.opChamfer","BLEND_VERTEX",VERTEX,{"blendedFrom":[makeQuery(id+"F5.opExtrude","CAP_EDGE",EDGE,{"disambiguationData":[OSD([subQ1])],"isStart":false}),makeQuery(id+"F5.opExtrude","CAP_EDGE",EDGE,{"disambiguationData":[OSD([subQ0])],"isStart":false}),makeQuery(id+"F5.opExtrude","CAP_FACE",FACE,{"disambiguationData":[OSD([subQ1,subQ0,sQuery(id+"F4.wireOp",EDGE,"E1.2"),sQuery(id+"F4.wireOp",EDGE,"E1.3"),sQuery(id+"F4.wireOp",EDGE,"E1.4")])],"isStart":true})],"blendedInto":[makeQuery(id+"F5.opExtrude","CAP_FACE",FACE,{"disambiguationData":[OSD([subQ1,subQ0,sQuery(id+"F4.wireOp",EDGE,"E1.2"),sQuery(id+"F4.wireOp",EDGE,"E1.3"),sQuery(id+"F4.wireOp",EDGE,"E1.4")])],"isStart":true})]});}
            cPlane(context, id + "F22", {"entities" : qUnion([Q0, Q1, Q2]), "cplaneType" : CPlaneType.THREE_POINT, "offset" : 150 * mm, "width" : 150 * mm, "height" : 150 * mm});
        }
        {
            var Q0;
            Q0=qCreatedBy(id+"F22.planeOp",FACE);
            var sketch = newSketch(context, id + "F23", { "sketchPlane" : qUnion([Q0])});
            skLineSegment(sketch, "E20", {"start": v(-6.63, -1.72) * mm, "end": v(-0.87, -10.5) * mm});
            skLineSegment(sketch, "E21", {"start": v(-0.87, -10.5) * mm, "end": v(6.26, -2.78) * mm});
            skLineSegment(sketch, "E22", {"start": v(6.26, -2.78) * mm, "end": v(-6.63, -1.72) * mm});
            skSolve(sketch);
        }
        {
            var Q0;
            {var subQ0=sQuery(id+"F0.wireOp",EDGE,"E0.2");var subQ1=sQuery(id+"F0.wireOp",EDGE,"E0.1");Q0=makeQuery(id+"F11.boolean.opBoolean","MERGE",VERTEX,{"derivedFrom":[makeQuery(id+"F2.opChamfer","BLEND_VERTEX",VERTEX,{"blendedFrom":[makeQuery(id+"F1.opExtrude","CAP_EDGE",EDGE,{"disambiguationData":[OSD([subQ1])],"isStart":false}),makeQuery(id+"F1.opExtrude","CAP_EDGE",EDGE,{"disambiguationData":[OSD([subQ0])],"isStart":false}),makeQuery(id+"F1.opExtrude","CAP_FACE",FACE,{"disambiguationData":[OSD([sQuery(id+"F0.wireOp",EDGE,"E0.0"),subQ1,subQ0,sQuery(id+"F0.wireOp",EDGE,"E0.3"),sQuery(id+"F0.wireOp",EDGE,"E0.4")])],"isStart":true})],"blendedInto":[makeQuery(id+"F1.opExtrude","CAP_FACE",FACE,{"disambiguationData":[OSD([sQuery(id+"F0.wireOp",EDGE,"E0.0"),subQ1,subQ0,sQuery(id+"F0.wireOp",EDGE,"E0.3"),sQuery(id+"F0.wireOp",EDGE,"E0.4")])],"isStart":true})]}),makeQuery(id+"F11.opLoft","MID_CAP_VERTEX",VERTEX,{"disambiguationData":[OSD([sQuery(id+"F8.wireOp",EDGE,"E3"),sQuery(id+"F8.wireOp",EDGE,"E4")])],"capPos":0.0})]});}
            var Q1;
            {var subQ0=sQuery(id+"F4.wireOp",EDGE,"E1.4");var subQ1=sQuery(id+"F4.wireOp",EDGE,"E1.3");Q1=makeQuery(id+"F6.opChamfer","BLEND_VERTEX",VERTEX,{"blendedFrom":[makeQuery(id+"F5.opExtrude","CAP_EDGE",EDGE,{"disambiguationData":[OSD([subQ1])],"isStart":false}),makeQuery(id+"F5.opExtrude","CAP_EDGE",EDGE,{"disambiguationData":[OSD([subQ0])],"isStart":false}),makeQuery(id+"F5.opExtrude","CAP_FACE",FACE,{"disambiguationData":[OSD([sQuery(id+"F4.wireOp",EDGE,"E1.0"),sQuery(id+"F4.wireOp",EDGE,"E1.1"),sQuery(id+"F4.wireOp",EDGE,"E1.2"),subQ1,subQ0])],"isStart":true})],"blendedInto":[makeQuery(id+"F5.opExtrude","CAP_FACE",FACE,{"disambiguationData":[OSD([sQuery(id+"F4.wireOp",EDGE,"E1.0"),sQuery(id+"F4.wireOp",EDGE,"E1.1"),sQuery(id+"F4.wireOp",EDGE,"E1.2"),subQ1,subQ0])],"isStart":true})]});}
            var Q2;
            Q2=makeQuery(id+"F11.opLoft","MID_CAP_VERTEX",VERTEX,{"disambiguationData":[OSD([sQuery(id+"F8.wireOp",EDGE,"E2"),sQuery(id+"F8.wireOp",EDGE,"E3")])],"capPos":0.0});
            cPlane(context, id + "F24", {"entities" : qUnion([Q0, Q1, Q2]), "cplaneType" : CPlaneType.THREE_POINT, "offset" : 150 * mm, "width" : 150 * mm, "height" : 150 * mm});
        }
        {
            var Q0;
            Q0=qCreatedBy(id+"F24.planeOp",FACE);
            var sketch = newSketch(context, id + "F25", { "sketchPlane" : qUnion([Q0])});
            skLineSegment(sketch, "E23", {"start": v(0.23, 2.78) * mm, "end": v(6, -6) * mm});
            skLineSegment(sketch, "E24", {"start": v(6, -6) * mm, "end": v(-6.9, -4.93) * mm});
            skLineSegment(sketch, "E25", {"start": v(-6.9, -4.93) * mm, "end": v(0.23, 2.78) * mm});
            skSolve(sketch);
        }
        {
            var Q0;
            Q0 = qSketchRegion(id + "F23", true);
            var Q1;
            Q1 = qSketchRegion(id + "F25", true);
            loft(context, id + "F26", {"sheetProfilesArray" : [{ "sheetProfileEntities" : qUnion([Q0]) }, { "sheetProfileEntities" : qUnion([Q1]) }]});
        }
        {
            var Q0;
            {var subQ0=sQuery(id+"F0.wireOp",EDGE,"E0.3");var subQ1=sQuery(id+"F0.wireOp",EDGE,"E0.2");Q0=makeQuery(id+"F11.boolean.opBoolean","MERGE",VERTEX,{"derivedFrom":[makeQuery(id+"F2.opChamfer","BLEND_VERTEX",VERTEX,{"blendedFrom":[makeQuery(id+"F1.opExtrude","CAP_EDGE",EDGE,{"disambiguationData":[OSD([subQ1])],"isStart":false}),makeQuery(id+"F1.opExtrude","CAP_EDGE",EDGE,{"disambiguationData":[OSD([subQ0])],"isStart":false}),makeQuery(id+"F1.opExtrude","CAP_FACE",FACE,{"disambiguationData":[OSD([sQuery(id+"F0.wireOp",EDGE,"E0.0"),sQuery(id+"F0.wireOp",EDGE,"E0.1"),subQ1,subQ0,sQuery(id+"F0.wireOp",EDGE,"E0.4")])],"isStart":true})],"blendedInto":[makeQuery(id+"F1.opExtrude","CAP_FACE",FACE,{"disambiguationData":[OSD([sQuery(id+"F0.wireOp",EDGE,"E0.0"),sQuery(id+"F0.wireOp",EDGE,"E0.1"),subQ1,subQ0,sQuery(id+"F0.wireOp",EDGE,"E0.4")])],"isStart":true})]}),makeQuery(id+"F11.opLoft","MID_CAP_VERTEX",VERTEX,{"disambiguationData":[OSD([sQuery(id+"F10.wireOp",EDGE,"E6"),sQuery(id+"F10.wireOp",EDGE,"E7")])],"capPos":1.0})]});}
            var Q1;
            {var subQ0=sQuery(id+"F0.wireOp",EDGE,"E0.2");var subQ1=sQuery(id+"F0.wireOp",EDGE,"E0.1");Q1=makeQuery(id+"F11.boolean.opBoolean","MERGE",VERTEX,{"derivedFrom":[makeQuery(id+"F2.opChamfer","BLEND_VERTEX",VERTEX,{"blendedFrom":[makeQuery(id+"F1.opExtrude","CAP_EDGE",EDGE,{"disambiguationData":[OSD([subQ1])],"isStart":false}),makeQuery(id+"F1.opExtrude","CAP_EDGE",EDGE,{"disambiguationData":[OSD([subQ0])],"isStart":false}),makeQuery(id+"F1.opExtrude","CAP_FACE",FACE,{"disambiguationData":[OSD([sQuery(id+"F0.wireOp",EDGE,"E0.0"),subQ1,subQ0,sQuery(id+"F0.wireOp",EDGE,"E0.3"),sQuery(id+"F0.wireOp",EDGE,"E0.4")])],"isStart":true})],"blendedInto":[makeQuery(id+"F1.opExtrude","CAP_FACE",FACE,{"disambiguationData":[OSD([sQuery(id+"F0.wireOp",EDGE,"E0.0"),subQ1,subQ0,sQuery(id+"F0.wireOp",EDGE,"E0.3"),sQuery(id+"F0.wireOp",EDGE,"E0.4")])],"isStart":true})]}),makeQuery(id+"F11.opLoft","MID_CAP_VERTEX",VERTEX,{"disambiguationData":[OSD([sQuery(id+"F8.wireOp",EDGE,"E3"),sQuery(id+"F8.wireOp",EDGE,"E4")])],"capPos":0.0})]});}
            var Q2;
            {var subQ0=sQuery(id+"F4.wireOp",EDGE,"E1.4");var subQ1=sQuery(id+"F4.wireOp",EDGE,"E1.3");Q2=makeQuery(id+"F6.opChamfer","BLEND_VERTEX",VERTEX,{"blendedFrom":[makeQuery(id+"F5.opExtrude","CAP_EDGE",EDGE,{"disambiguationData":[OSD([subQ1])],"isStart":false}),makeQuery(id+"F5.opExtrude","CAP_EDGE",EDGE,{"disambiguationData":[OSD([subQ0])],"isStart":false}),makeQuery(id+"F5.opExtrude","CAP_FACE",FACE,{"disambiguationData":[OSD([sQuery(id+"F4.wireOp",EDGE,"E1.0"),sQuery(id+"F4.wireOp",EDGE,"E1.1"),sQuery(id+"F4.wireOp",EDGE,"E1.2"),subQ1,subQ0])],"isStart":true})],"blendedInto":[makeQuery(id+"F5.opExtrude","CAP_FACE",FACE,{"disambiguationData":[OSD([sQuery(id+"F4.wireOp",EDGE,"E1.0"),sQuery(id+"F4.wireOp",EDGE,"E1.1"),sQuery(id+"F4.wireOp",EDGE,"E1.2"),subQ1,subQ0])],"isStart":true})]});}
            cPlane(context, id + "F27", {"entities" : qUnion([Q0, Q1, Q2]), "cplaneType" : CPlaneType.THREE_POINT, "offset" : 150 * mm, "width" : 150 * mm, "height" : 150 * mm});
        }
        {
            var Q0;
            Q0=qCreatedBy(id+"F27.planeOp",FACE);
            var sketch = newSketch(context, id + "F28", { "sketchPlane" : qUnion([Q0])});
            skLineSegment(sketch, "E26", {"start": v(-5.95, -3.4) * mm, "end": v(1.91, -10.36) * mm});
            skLineSegment(sketch, "E27", {"start": v(1.91, -10.36) * mm, "end": v(6.77, -1.05) * mm});
            skLineSegment(sketch, "E28", {"start": v(6.77, -1.05) * mm, "end": v(-5.95, -3.4) * mm});
            skSolve(sketch);
        }
        {
            var Q0;
            {var subQ0=sQuery(id+"F0.wireOp",EDGE,"E0.4");var subQ1=sQuery(id+"F0.wireOp",EDGE,"E0.0");Q0=makeQuery(id+"F2.opChamfer","BLEND_VERTEX",VERTEX,{"blendedFrom":[makeQuery(id+"F1.opExtrude","CAP_EDGE",EDGE,{"disambiguationData":[OSD([subQ1])],"isStart":false}),makeQuery(id+"F1.opExtrude","CAP_EDGE",EDGE,{"disambiguationData":[OSD([subQ0])],"isStart":false}),makeQuery(id+"F1.opExtrude","CAP_FACE",FACE,{"disambiguationData":[OSD([subQ1,sQuery(id+"F0.wireOp",EDGE,"E0.1"),sQuery(id+"F0.wireOp",EDGE,"E0.2"),sQuery(id+"F0.wireOp",EDGE,"E0.3"),subQ0])],"isStart":true})],"blendedInto":[makeQuery(id+"F1.opExtrude","CAP_FACE",FACE,{"disambiguationData":[OSD([subQ1,sQuery(id+"F0.wireOp",EDGE,"E0.1"),sQuery(id+"F0.wireOp",EDGE,"E0.2"),sQuery(id+"F0.wireOp",EDGE,"E0.3"),subQ0])],"isStart":true})]});}
            var Q1;
            {var subQ0=sQuery(id+"F4.wireOp",EDGE,"E1.2");var subQ1=sQuery(id+"F4.wireOp",EDGE,"E1.1");Q1=makeQuery(id+"F6.opChamfer","BLEND_VERTEX",VERTEX,{"blendedFrom":[makeQuery(id+"F5.opExtrude","CAP_EDGE",EDGE,{"disambiguationData":[OSD([subQ1])],"isStart":false}),makeQuery(id+"F5.opExtrude","CAP_EDGE",EDGE,{"disambiguationData":[OSD([subQ0])],"isStart":false}),makeQuery(id+"F5.opExtrude","CAP_FACE",FACE,{"disambiguationData":[OSD([sQuery(id+"F4.wireOp",EDGE,"E1.0"),subQ1,subQ0,sQuery(id+"F4.wireOp",EDGE,"E1.3"),sQuery(id+"F4.wireOp",EDGE,"E1.4")])],"isStart":true})],"blendedInto":[makeQuery(id+"F5.opExtrude","CAP_FACE",FACE,{"disambiguationData":[OSD([sQuery(id+"F4.wireOp",EDGE,"E1.0"),subQ1,subQ0,sQuery(id+"F4.wireOp",EDGE,"E1.3"),sQuery(id+"F4.wireOp",EDGE,"E1.4")])],"isStart":true})]});}
            var Q2;
            {var subQ0=sQuery(id+"F4.wireOp",EDGE,"E1.1");var subQ1=sQuery(id+"F4.wireOp",EDGE,"E1.0");Q2=makeQuery(id+"F6.opChamfer","BLEND_VERTEX",VERTEX,{"blendedFrom":[makeQuery(id+"F5.opExtrude","CAP_EDGE",EDGE,{"disambiguationData":[OSD([subQ1])],"isStart":false}),makeQuery(id+"F5.opExtrude","CAP_EDGE",EDGE,{"disambiguationData":[OSD([subQ0])],"isStart":false}),makeQuery(id+"F5.opExtrude","CAP_FACE",FACE,{"disambiguationData":[OSD([subQ1,subQ0,sQuery(id+"F4.wireOp",EDGE,"E1.2"),sQuery(id+"F4.wireOp",EDGE,"E1.3"),sQuery(id+"F4.wireOp",EDGE,"E1.4")])],"isStart":true})],"blendedInto":[makeQuery(id+"F5.opExtrude","CAP_FACE",FACE,{"disambiguationData":[OSD([subQ1,subQ0,sQuery(id+"F4.wireOp",EDGE,"E1.2"),sQuery(id+"F4.wireOp",EDGE,"E1.3"),sQuery(id+"F4.wireOp",EDGE,"E1.4")])],"isStart":true})]});}
            cPlane(context, id + "F29", {"entities" : qUnion([Q0, Q1, Q2]), "cplaneType" : CPlaneType.THREE_POINT, "offset" : 150 * mm, "width" : 150 * mm, "height" : 150 * mm});
        }
        {
            var Q0;
            Q0=qCreatedBy(id+"F29.planeOp",FACE);
            var sketch = newSketch(context, id + "F30", { "sketchPlane" : qUnion([Q0])});
            skLineSegment(sketch, "E29", {"start": v(-0.5, 2.75) * mm, "end": v(7.35, -4.21) * mm});
            skLineSegment(sketch, "E30", {"start": v(7.35, -4.21) * mm, "end": v(-5.36, -6.56) * mm});
            skLineSegment(sketch, "E31", {"start": v(-5.36, -6.56) * mm, "end": v(-0.5, 2.75) * mm});
            skSolve(sketch);
        }
        {
            var Q0;
            Q0 = qSketchRegion(id + "F28", true);
            var Q1;
            Q1 = qSketchRegion(id + "F30", true);
            loft(context, id + "F31", {"sheetProfilesArray" : [{ "sheetProfileEntities" : qUnion([Q0]) }, { "sheetProfileEntities" : qUnion([Q1]) }]});
        }
    });
